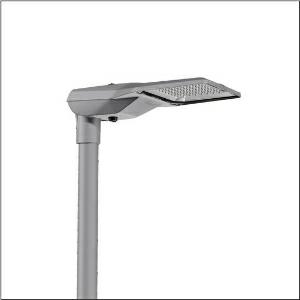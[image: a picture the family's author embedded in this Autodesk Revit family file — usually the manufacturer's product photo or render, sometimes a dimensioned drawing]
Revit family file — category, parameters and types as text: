
# Revit family: streetlight_sl_21_midi___p0_8a_5xe3u33t08lb_3dc7
name_source: partatom
category: Lighting Fixtures
units: mm (PartAtom-declared; Revit-internal decimal feet)

## family parameters
Cut with Voids When Loaded = No
Host = Face
Light Source = No
Part Type = Normal
Room Calculation Point = No
Round Connector Dimension = Use Diameter
Shared = No

## types (1)
- --- (1 x LED, 14470 lm, 99.6 W, 3000K)
    Apparent Load = 100 VA
    CIE Flux Codes = 33 69 96 100 100
    Color Rendering = 70
    Color Temperature = 3000K
    Default Elevation = 1800 mm
    Description = Streetlight SL 21 midi, mast luminaire, primary light control with lens, of PMMA, primary optical cover: cover, of toughened safety glass, transparent, light distribution: P0.8a, light emission: direct distribution, primary light characteristic: asymmetric, installation type: post-top, side-entry, LED, High Power LED, rated luminous flux: 14.470lm, luminous efficacy: 145lm/W, light colour: 730, colour temperature: 3000K, control gear: D4i, control: pre-setting: logarithmic dimming characteristic, flexible luminous flux parameterisation, time-dependent luminous flux control, constant luminous flux control, overheat protection, mains connection: 230..240V, AC, 50/60Hz, start of lifetime: 100W, end of service life: 102W, reduction: 46W, luminaire housing, of diecast aluminium, powder-coated, SITECO metallic grey (DB 702S), corrosivity category C5 high according to DIN EN ISO 12944, multi-level sealing system, sealing non-destructively replaceable, inclination adjustable: 0°, 5°, 10°, 15°, please order mast flange separately, length: 644mm, width: 335mm, height: 110mm, mast flange for spigot size: 42mm (side-entry): 5XC10008XM4, 60/48mm (side-entry/post-top): 5XC10108XM2, 76/60mm (side-entry/post-top): 5XC10108XM1, mounting height: 4..8m, Smart Interface below and above, protection rating (complete): IP66, insulation class (complete): insulation class II (safety insulation), certification: CE, ENEC, ENEC+, VDE, impact resistance: IK10, permissible operating ambient temperature for outdoor applications: -40..+50°C, standard-compliant lighting for roads and squares, packaging unit: 1 piece

Light Distribution: P0.8a
    Height = 111 mm
    Lamp = 1 x LED
    Lamp Light Flux = 14470 lm
    Lamp Power = 99.6 W
    Lamp count = 1
    Length = 644 mm
    Luminous efficacy = 145 lm/W
    Manufacturer = Siteco
    ModVariant = No
    Model = 5XE3U33T08LB
    Number of Poles = 1
    OnlyDefault = Yes
    Power Factor = 1
    Product Name = Streetlight SL 21 midi | P0.8a
    Product group = mast luminaire | pylon top
    ProductGroupID = 6100
    Protection Class = Protection class II
    Protection Degree = IP 66
    RLX_Detail_Level = 1
    RLX_Emergency_Light_Flux = 0 lm
    RLX_Emergency_Type = 0
    RLX_Emergency_Type_DB = No
    RlxData = <blob elided: 26729 chars, md5=bc6ff0ad>
    Socket = socket
    Standby Power = 0 W
    System Light Flux = 14470 lm
    System Power = 100 W
    Type Comments = factory setting: luminous flux: 100 % | dim-lin: 254 | 1020 mA
    Type Image = l_1004304.jpg
    URL = http://relux.com
    VarID = @adj_033153
    Voltage = 0 V
    Weight = 0.00 kg
    Width = 336 mm

## geometry (parser evidence)
native form markers: Blend x4, Sweep x10
no freeform markers — native parametric forms only
